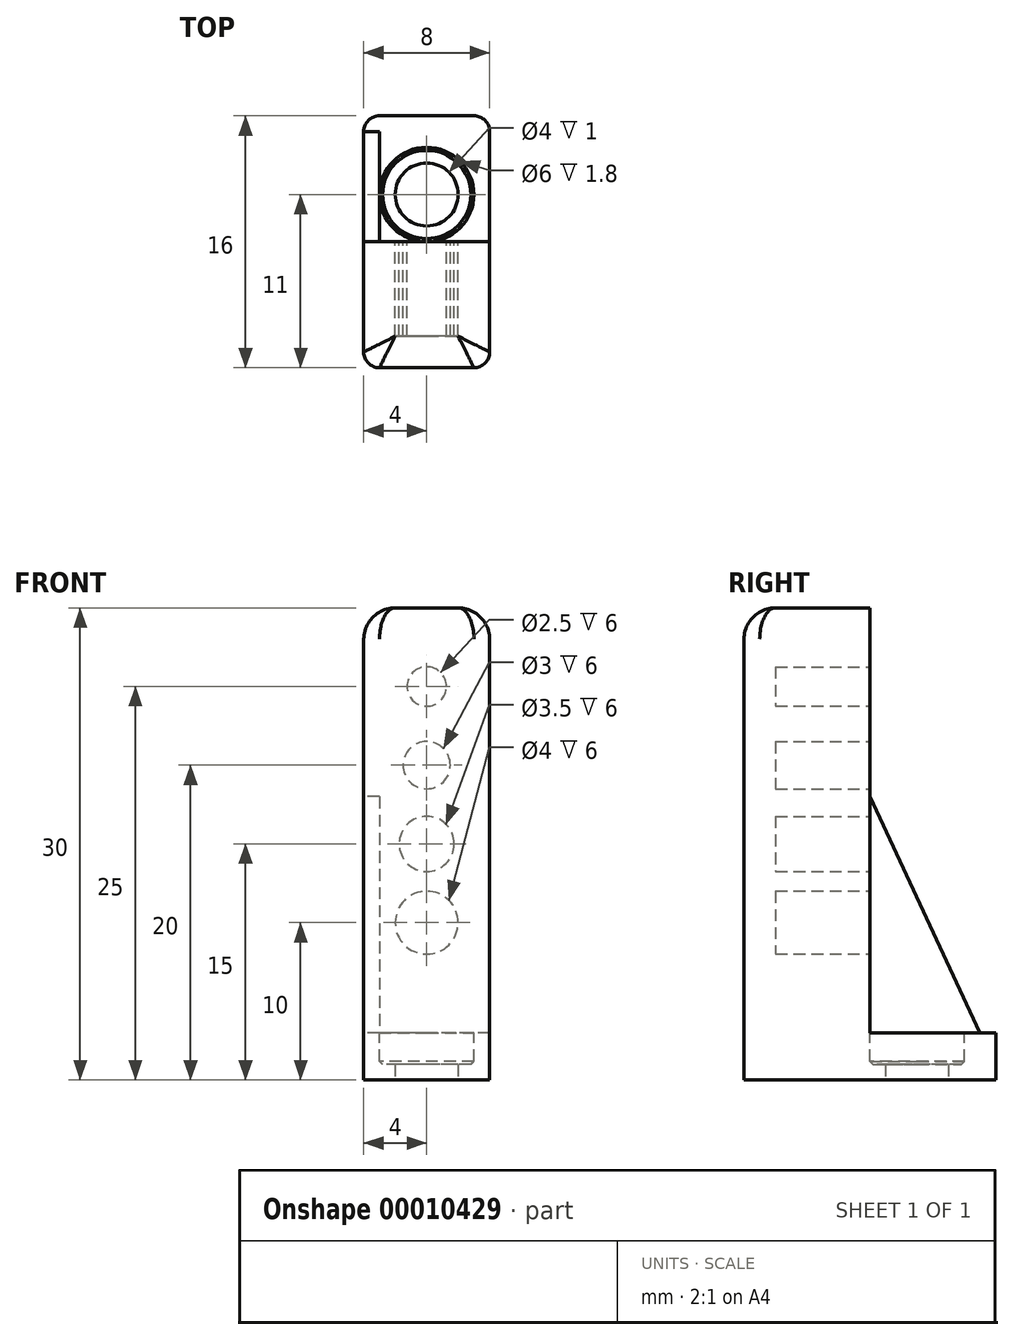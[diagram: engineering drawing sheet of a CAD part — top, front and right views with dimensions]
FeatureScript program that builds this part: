
annotation { "Feature Type Name" : "Feature", "Feature Type Description" : "" }
export const myFeature = defineFeature(function(context is Context, id is Id, definition is map)
    precondition{}
    {
        {
            var Q0;
            Q0=qCreatedBy(makeId("Top.planeOp"),FACE);
            var sketch = newSketch(context, id + "F0", { "sketchPlane" : qUnion([Q0])});
            skLineSegment(sketch, "E0.bottom", {"start": v(3, 5) * mm, "end": v(-3, 5) * mm});
            skLineSegment(sketch, "E0.top", {"start": v(4, -5) * mm, "end": v(-4, -5) * mm});
            skLineSegment(sketch, "E0.left", {"start": v(4, 4) * mm, "end": v(4, -5) * mm});
            skLineSegment(sketch, "E0.right", {"start": v(-4, 4) * mm, "end": v(-4, -5) * mm});
            skPoint(sketch, "E0.middle", {"position": v(0, 0) * mm});
            skCircle(sketch, "E1", {"center": v(0, 0) * mm, "radius": 2 * mm});
            skPoint(sketch, "E2.visualSharp", {"position": v(-4, 5) * mm});
            skArc(sketch, "E2.filletArc", {"start": v(-3, 5) * mm, "mid": v(-3.7, 4.7) * mm, "end": v(-4, 4) * mm});
            skPoint(sketch, "E3.visualSharp", {"position": v(4, 5) * mm});
            skArc(sketch, "E3.filletArc", {"start": v(4, 4) * mm, "mid": v(3.7, 4.7) * mm, "end": v(3, 5) * mm});
            skSolve(sketch);
        }
        {
            var Q0;
            Q0=makeQuery(id+"F0.imprint","IMPRINT",FACE,{"disambiguationData":[TD([[makeQuery(id+"F0.imprint","IMPRINT",EDGE,{"derivedFrom":sQuery(id+"F0.wireOp",EDGE,"E0.bottom")}),1.0]])]});
            extrude(context, id + "F1", {"entities" : qUnion([Q0]), "depth" : 3 * mm});
        }
        {
            var Q0;
            Q0=qCreatedBy(makeId("Top.planeOp"),FACE);
            var sketch = newSketch(context, id + "F2", { "sketchPlane" : qUnion([Q0])});
            skLineSegment(sketch, "E4.top", {"start": v(-4, -3) * mm, "end": v(4, -3) * mm});
            skLineSegment(sketch, "E4.left", {"start": v(-4, -10) * mm, "end": v(-4, -3) * mm});
            skLineSegment(sketch, "E4.right", {"start": v(4, -10) * mm, "end": v(4, -3) * mm});
            skLineSegment(sketch, "E5", {"start": v(-3, -11) * mm, "end": v(3, -11) * mm});
            skPoint(sketch, "E6.visualSharp", {"position": v(-4, -11) * mm});
            skArc(sketch, "E6.filletArc", {"start": v(-4, -10) * mm, "mid": v(-3.7, -10.7) * mm, "end": v(-3, -11) * mm});
            skPoint(sketch, "E7.visualSharp", {"position": v(4, -11) * mm});
            skArc(sketch, "E7.filletArc", {"start": v(3, -11) * mm, "mid": v(3.7, -10.7) * mm, "end": v(4, -10) * mm});
            skSolve(sketch);
        }
        {
            var Q0;
            Q0=qSketchRegion(id+"F2",true);
            extrude(context, id + "F3", {"entities" : qUnion([Q0]), "operationType" : NewBodyOperationType.ADD, "depth" : 30 * mm});
        }
        {
            var Q0;
            Q0=makeQuery(id+"F3.boolean.opBoolean","MERGE",FACE,{"derivedFrom":[makeQuery(id+"F1.opExtrude","SWEPT_FACE",FACE,{"disambiguationData":[OSD([sQuery(id+"F0.wireOp",EDGE,"E0.right")])]}),makeQuery(id+"F3.opExtrude","SWEPT_FACE",FACE,{"disambiguationData":[OSD([sQuery(id+"F2.wireOp",EDGE,"E4.left")])]})]});
            var sketch = newSketch(context, id + "F4", { "sketchPlane" : qUnion([Q0])});
            skLineSegment(sketch, "E8", {"start": v(-4, 3) * mm, "end": v(3, 18) * mm});
            skLineSegment(sketch, "E9", {"start": v(3, 18) * mm, "end": v(3, 3) * mm});
            skLineSegment(sketch, "E10", {"start": v(3, 3) * mm, "end": v(-4, 3) * mm});
            skSolve(sketch);
        }
        {
            var Q0;
            Q0=qSketchRegion(id+"F4",true);
            extrude(context, id + "F5", {"entities" : qUnion([Q0]), "operationType" : NewBodyOperationType.ADD, "oppositeDirection" : true, "depth" : 1 * mm});
        }
        {
            var Q0;
            Q0=makeQuery(id+"F3.opExtrude","SWEPT_FACE",FACE,{"disambiguationData":[OSD([sQuery(id+"F2.wireOp",EDGE,"E4.top")])]});
            var sketch = newSketch(context, id + "F6", { "sketchPlane" : qUnion([Q0])});
            skCircle(sketch, "E11", {"center": v(0, 10) * mm, "radius": 2 * mm});
            skCircle(sketch, "E12", {"center": v(0, 15) * mm, "radius": 1.75 * mm});
            skCircle(sketch, "E13", {"center": v(0, 20) * mm, "radius": 1.5 * mm});
            skCircle(sketch, "E14", {"center": v(0, 25) * mm, "radius": 1.25 * mm});
            skSolve(sketch);
        }
        {
            var Q0;
            Q0=qSketchRegion(id+"F6",true);
            extrude(context, id + "F7", {"entities" : qUnion([Q0]), "operationType" : NewBodyOperationType.REMOVE, "oppositeDirection" : true, "depth" : 6 * mm});
        }
        {
            var Q0;
            Q0=makeQuery(id+"F3.opExtrude","CAP_EDGE",EDGE,{"disambiguationData":[OSD([sQuery(id+"F2.wireOp",EDGE,"E4.left")])],"isStart":false});
            var Q1;
            Q1=makeQuery(id+"F3.opExtrude","CAP_EDGE",EDGE,{"disambiguationData":[OSD([sQuery(id+"F2.wireOp",EDGE,"E4.right")])],"isStart":false});
            var Q2;
            Q2=makeQuery(id+"F3.opExtrude","CAP_EDGE",EDGE,{"disambiguationData":[OSD([sQuery(id+"F2.wireOp",EDGE,"E6.filletArc")])],"isStart":false});
            fillet(context, id + "F8", {"entities" : qUnion([Q0, Q1, Q2]), "radius" : 2 * mm, "tangentPropagation" : true, "allowEdgeOverflow" : false});
        }
        {
            var Q0;
            Q0=makeQuery(id+"F1.opExtrude","CAP_FACE",FACE,{"disambiguationData":[OSD([sQuery(id+"F0.wireOp",EDGE,"E0.bottom"),sQuery(id+"F0.wireOp",EDGE,"E0.top"),sQuery(id+"F0.wireOp",EDGE,"E0.left"),sQuery(id+"F0.wireOp",EDGE,"E0.right"),sQuery(id+"F0.wireOp",EDGE,"E1"),sQuery(id+"F0.wireOp",EDGE,"E2.filletArc"),sQuery(id+"F0.wireOp",EDGE,"E3.filletArc")])],"isStart":false});
            var sketch = newSketch(context, id + "F9", { "sketchPlane" : qUnion([Q0])});
            skCircle(sketch, "E15", {"center": v(0, 0) * mm, "radius": 3 * mm});
            skSolve(sketch);
        }
        {
            var Q0;
            Q0=qSketchRegion(id+"F9",true);
            extrude(context, id + "F10", {"entities" : qUnion([Q0]), "operationType" : NewBodyOperationType.REMOVE, "oppositeDirection" : true, "depth" : 2 * mm});
        }
        {
            var Q0;
            Q0=makeQuery(id+"F10.boolean.opBoolean","COPY",EDGE,{"derivedFrom":makeQuery(id+"F10.opExtrude","CAP_EDGE",EDGE,{"disambiguationData":[OSD([sQuery(id+"F9.wireOp",EDGE,"E15")])],"isStart":false})});
            chamfer(context, id + "F11", {"entities" : qUnion([Q0]), "width" : .2 * mm, "tangentPropagation" : true});
        }
    });
